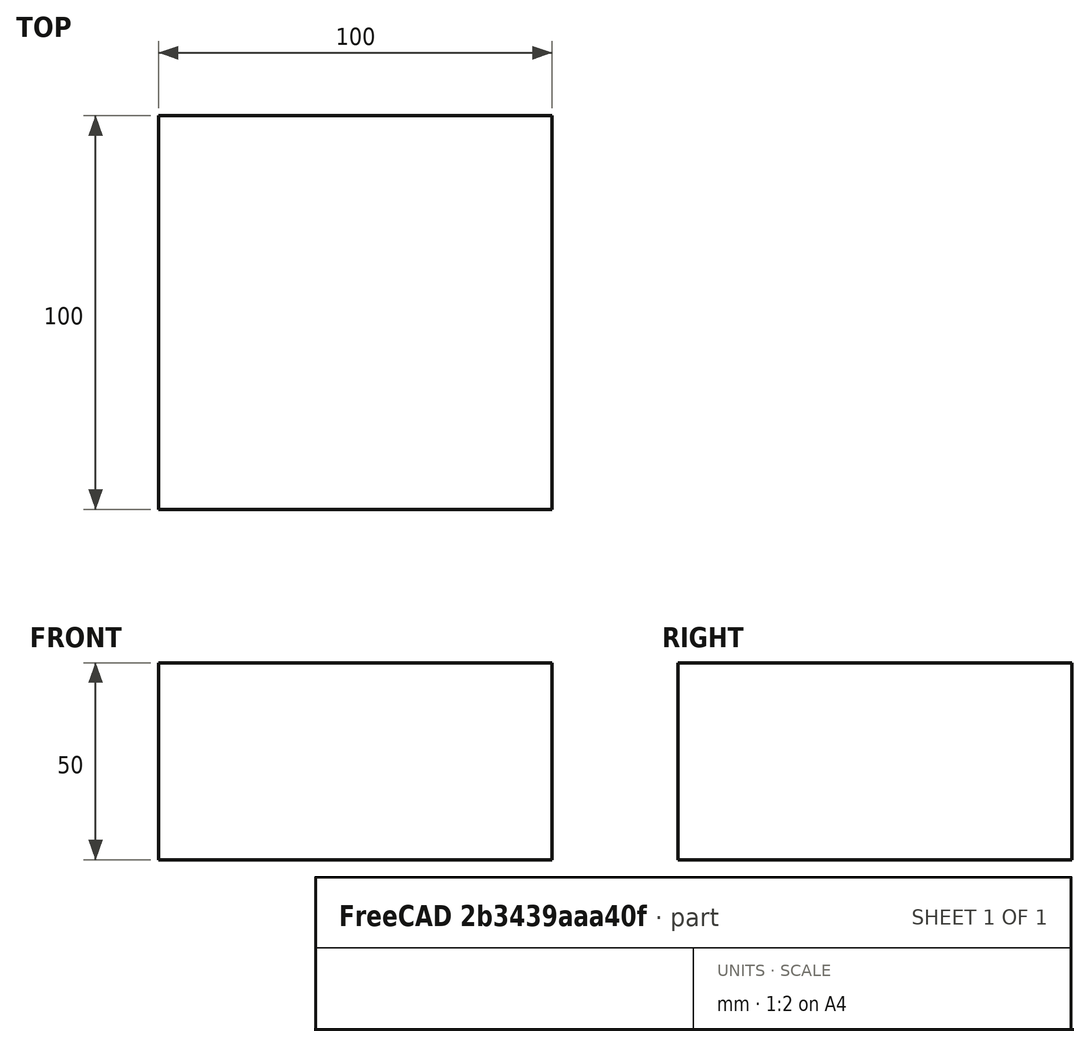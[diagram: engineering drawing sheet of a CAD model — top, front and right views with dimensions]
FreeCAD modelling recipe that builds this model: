
FCSTD DOCUMENT  (FreeCAD 0.15R4671 (Git))
Label: Square Bar 100 EN10059 S235JR
License: All rights reserved
LicenseURL: http://en.wikipedia.org/wiki/All_rights_reserved
objects: Sketcher::SketchObject×1, Part::Extrusion×1
note: 2 computed .brp shape members not serialized (recipe doc carries the construction recipe); baked Part::Feature solids carry a one-line shape summary decoded from their .brp

FEATURE [Sketcher::SketchObject] Sketch
  sketch-geometry (4):
    g0: LineSegment StartX=-50 StartY=-50 StartZ=0 EndX=50 EndY=-50 EndZ=0
    g1: LineSegment StartX=50 StartY=-50 StartZ=0 EndX=50 EndY=50 EndZ=0
    g2: LineSegment StartX=50 StartY=50 StartZ=0 EndX=-50 EndY=50 EndZ=0
    g3: LineSegment StartX=-50 StartY=50 StartZ=0 EndX=-50 EndY=-50 EndZ=0
  constraints (12):
    c: Coincident(g0,g1)
    c: Coincident(g1,g2)
    c: Coincident(g2,g3)
    c: Coincident(g3,g0)
    c: Horizontal(g0)
    c: Horizontal(g2)
    c: Vertical(g1)
    c: Vertical(g3)
    c: Symmetric(g1,g0,g-1)
    c: Symmetric(g2,g1,g-2)
    c: Equal(g1,g2)
    c: DistanceY(g1) = 100
FEATURE [Part::Extrusion] Extrude  label="Square Bar 100 EN10059 S235JR"
  Base = -> Sketch
  Dir = (0,0,50)
  Solid = true
